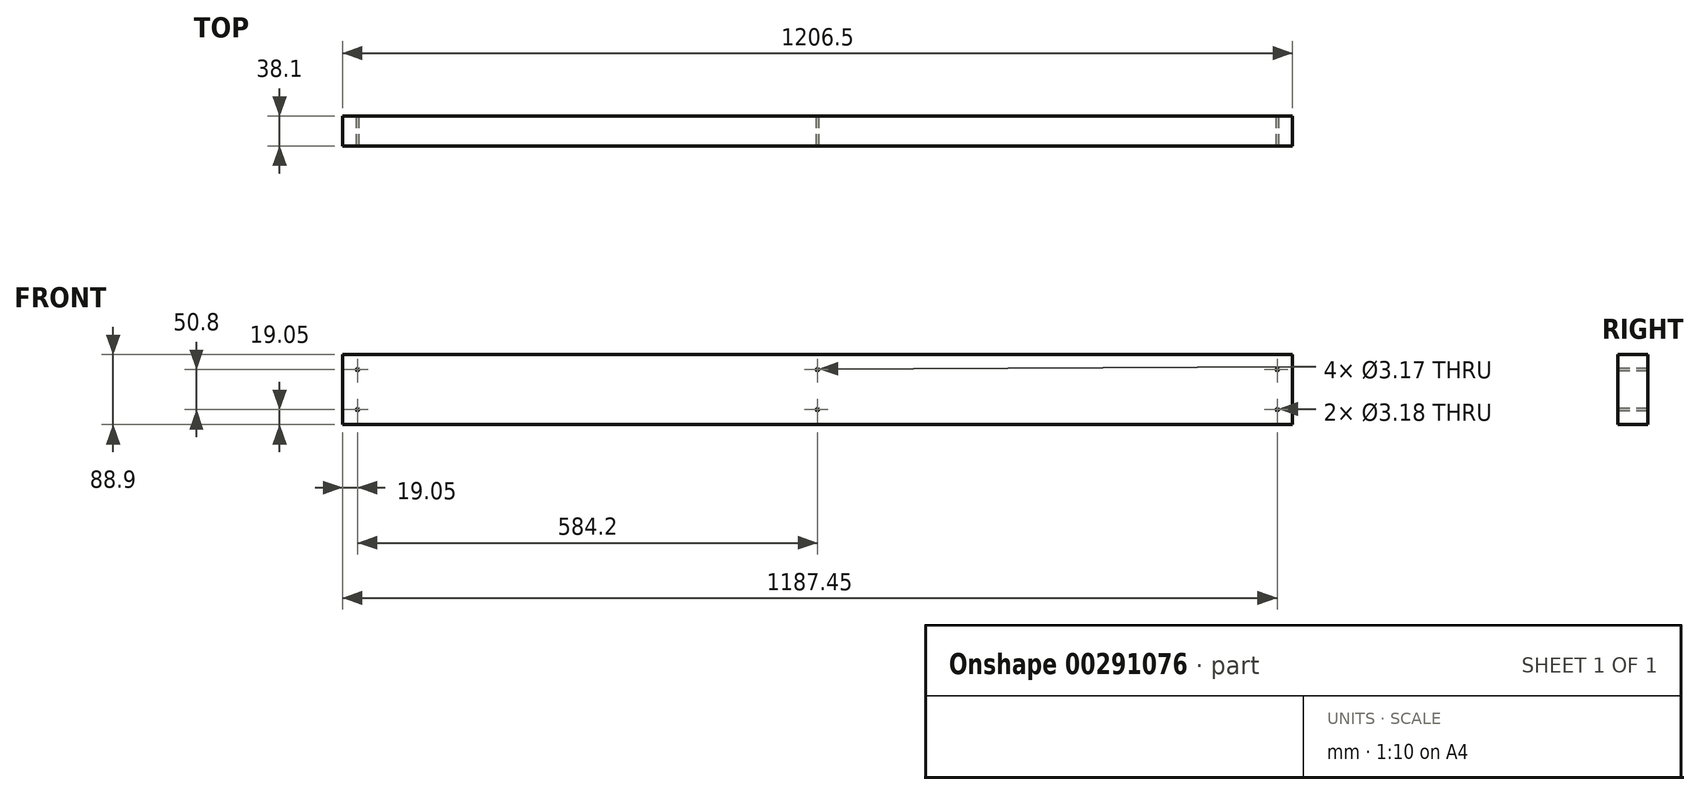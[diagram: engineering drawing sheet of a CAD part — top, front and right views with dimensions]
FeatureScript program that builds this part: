
annotation { "Feature Type Name" : "Feature", "Feature Type Description" : "" }
export const myFeature = defineFeature(function(context is Context, id is Id, definition is map)
    precondition{}
    {
        {
            var Q0;
            Q0=qCreatedBy(makeId("Front.planeOp"),FACE);
            var sketch = newSketch(context, id + "F0", { "sketchPlane" : qUnion([Q0])});
            skLineSegment(sketch, "E0.bottom", {"start": v(0, 0) * mm, "end": v(1206.5, 0) * mm});
            skLineSegment(sketch, "E0.top", {"start": v(0, -88.9) * mm, "end": v(1206.5, -88.9) * mm});
            skLineSegment(sketch, "E0.left", {"start": v(0, 0) * mm, "end": v(0, -88.9) * mm});
            skLineSegment(sketch, "E0.right", {"start": v(1206.5, 0) * mm, "end": v(1206.5, -88.9) * mm});
            skSolve(sketch);
        }
        {
            var Q0;
            Q0 = qSketchRegion(id + "F0", true);
            extrude(context, id + "F1", {"entities" : qUnion([Q0]), "oppositeDirection" : true, "depth" : 38.1 * mm});
        }
        {
            var Q0;
            Q0=qCreatedBy(makeId("Front.planeOp"),FACE);
            var sketch = newSketch(context, id + "F2", { "sketchPlane" : qUnion([Q0])});
            skCircle(sketch, "E1", {"center": v(19.05, -19.05) * mm, "radius": 1.59 * mm});
            skCircle(sketch, "E2.0.1.0", {"center": v(19.05, -69.85) * mm, "radius": 1.59 * mm});
            skCircle(sketch, "E2.1.0.0", {"center": v(603.25, -19.05) * mm, "radius": 1.59 * mm});
            skCircle(sketch, "E2.1.1.0", {"center": v(603.25, -69.85) * mm, "radius": 1.59 * mm});
            skCircle(sketch, "E2.2.0.0", {"center": v(1187.45, -19.05) * mm, "radius": 1.59 * mm});
            skCircle(sketch, "E2.2.1.0", {"center": v(1187.45, -69.85) * mm, "radius": 1.59 * mm});
            skLineSegment(sketch, "E2.direction1", {"start": v(19.05, -19.05) * mm, "end": v(603.25, -19.05) * mm, "construction": true});
            skLineSegment(sketch, "E2.direction2", {"start": v(19.05, -19.05) * mm, "end": v(19.05, -69.85) * mm, "construction": true});
            skSolve(sketch);
        }
        {
            var Q0;
            Q0 = qSketchRegion(id + "F2", true);
            extrude(context, id + "F3", {"entities" : qUnion([Q0]), "operationType" : NewBodyOperationType.REMOVE, "endBound" : BoundingType.THROUGH_ALL, "oppositeDirection" : true, "depth" : 25.4 * mm});
        }
    });
